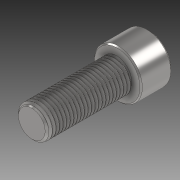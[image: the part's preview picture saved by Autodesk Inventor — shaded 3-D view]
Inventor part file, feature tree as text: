
AUTODESK INVENTOR PART (.ipt)
format: ipt  version: 2020 (Build 240168000, 168)  size: 438,784 bytes
history: mixed  units: in
note: dims shown in document units (in); Inventor stores cm internally (conversion verified against a paired STEP export)
features: chamfer x1, imported_body x1
ambient origin geometry x8: Origin, YZ Plane, XZ Plane, XY Plane, X Axis, Y Axis, Z Axis, Center Point
bodies: Solid1 (imported_parasolid)
feature tree (2):
  chamfer  "Chamfer2"  [1 undecoded]
  imported_body  NMx_Import_Brep_tag  [imported B-rep: ~5 faces, bbox_mm=None]
note: 1 required parameter value undecoded (feature->parameter linkage not recoverable at this tier; creation-order binding heuristic only, values carry confidence <= 0.55)
